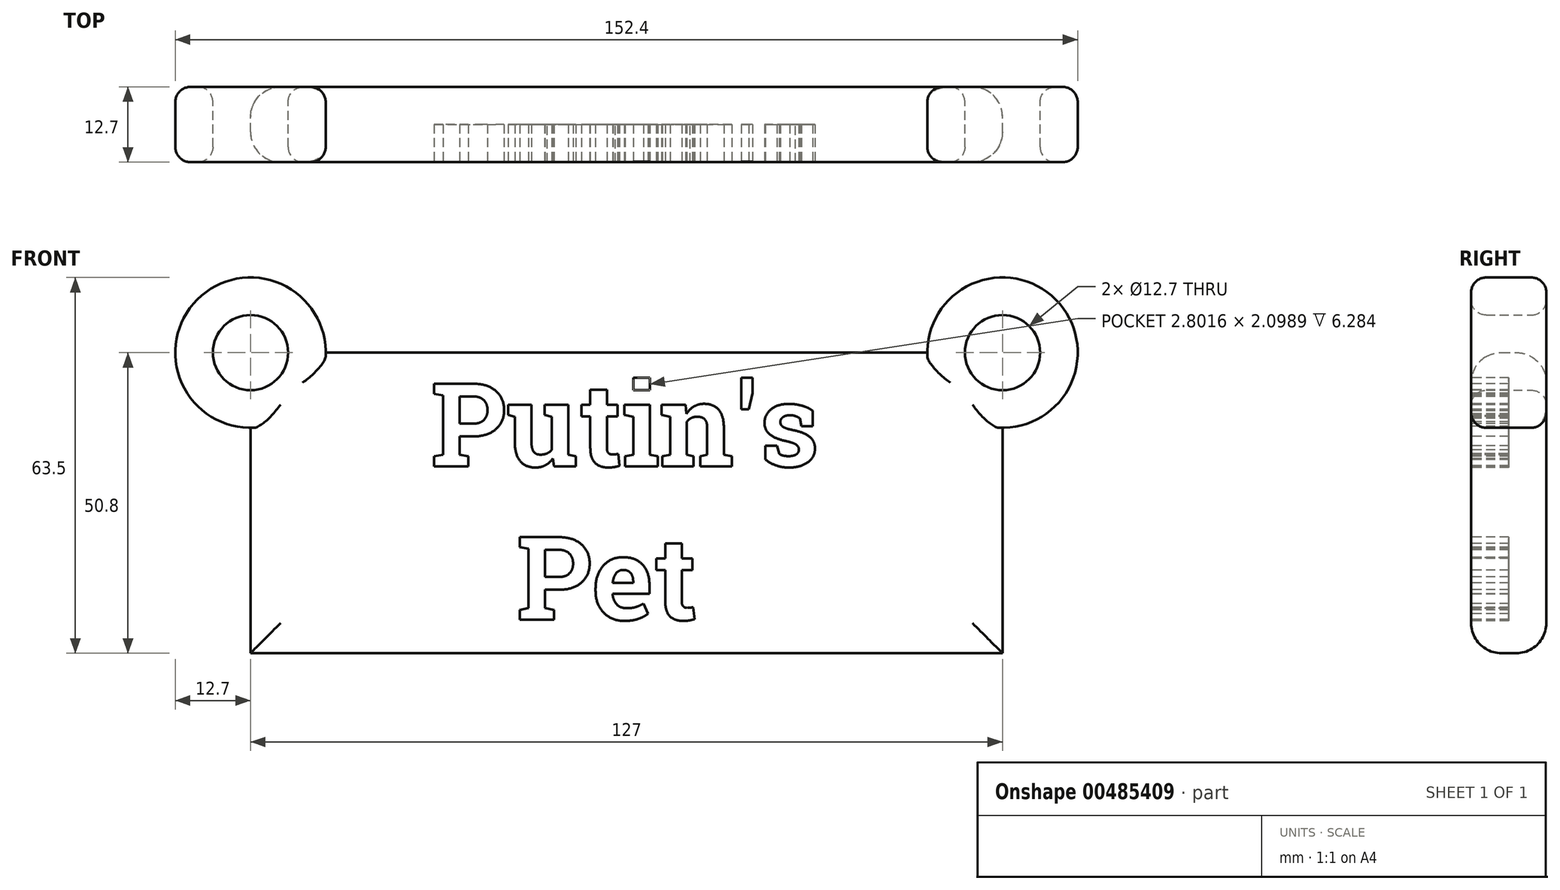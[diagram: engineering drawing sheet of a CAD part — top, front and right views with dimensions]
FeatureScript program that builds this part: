
annotation { "Feature Type Name" : "Feature", "Feature Type Description" : "" }
export const myFeature = defineFeature(function(context is Context, id is Id, definition is map)
    precondition{}
    {
        {
            var Q0;
            Q0=qCreatedBy(makeId("Front.planeOp"),FACE);
            var sketch = newSketch(context, id + "F0", { "sketchPlane" : qUnion([Q0])});
            skLineSegment(sketch, "E0.bottom", {"start": v(-127, 50.8) * mm, "end": v(0, 50.8) * mm});
            skLineSegment(sketch, "E0.top", {"start": v(-127, 0) * mm, "end": v(0, 0) * mm});
            skLineSegment(sketch, "E0.left", {"start": v(-127, 50.8) * mm, "end": v(-127, 0) * mm});
            skLineSegment(sketch, "E0.right", {"start": v(0, 50.8) * mm, "end": v(0, 0) * mm});
            skCircle(sketch, "E1", {"center": v(-127, 50.8) * mm, "radius": 6.35 * mm});
            skCircle(sketch, "E2", {"center": v(0, 50.8) * mm, "radius": 12.7 * mm});
            skCircle(sketch, "E3", {"center": v(0, 50.8) * mm, "radius": 6.35 * mm});
            skCircle(sketch, "E4", {"center": v(-127, 50.8) * mm, "radius": 12.7 * mm});
            skSolve(sketch);
        }
        {
            var Q0;
            Q0=qSketchRegion(id+"F0",true);
            extrude(context, id + "F1", {"entities" : qUnion([Q0]), "depth" : 12.7 * mm});
        }
        {
            var Q0;
            Q0=makeQuery(id+"F1.opExtrude","CAP_FACE",FACE,{"disambiguationData":[OSD([sQuery(id+"F0.wireOp",EDGE,"E0.bottom"),sQuery(id+"F0.wireOp",EDGE,"E0.top"),sQuery(id+"F0.wireOp",EDGE,"E0.left"),sQuery(id+"F0.wireOp",EDGE,"E0.right"),sQuery(id+"F0.wireOp",EDGE,"E1"),sQuery(id+"F0.wireOp",EDGE,"E2"),sQuery(id+"F0.wireOp",EDGE,"E3"),sQuery(id+"F0.wireOp",EDGE,"E4")])],"isStart":false});
            var sketch = newSketch(context, id + "F2", { "sketchPlane" : qUnion([Q0])});
            skText(sketch, "E5", { "text": "Putin\'s \n   Pet", "fontName": "RobotoSlab-Bold.ttf"});
            const initialGuessF2  = {"E5": [-0.09652, 0.03158, 1, 0, 0.01414]};
            skSetInitialGuess(sketch, initialGuessF2);
            skSolve(sketch);
        }
        {
            var Q0;
            Q0=qSketchRegion(id+"F2",true);
            extrude(context, id + "F3", {"entities" : qUnion([Q0]), "operationType" : NewBodyOperationType.REMOVE, "oppositeDirection" : true, "depth" : 6.35 * mm});
        }
        {
            var Q0;
            Q0=makeQuery(id+"F1.opExtrude","CAP_EDGE",EDGE,{"disambiguationData":[OSD([sQuery(id+"F0.wireOp",EDGE,"E1")])],"isStart":false});
            var Q1;
            Q1=makeQuery(id+"F1.opExtrude","CAP_EDGE",EDGE,{"disambiguationData":[OSD([sQuery(id+"F0.wireOp",EDGE,"E3")])],"isStart":false});
            var Q2;
            Q2=makeQuery(id+"F1.opExtrude","CAP_EDGE",EDGE,{"disambiguationData":[OSD([sQuery(id+"F0.wireOp",EDGE,"E1")])],"isStart":true});
            var Q3;
            Q3=makeQuery(id+"F1.opExtrude","CAP_EDGE",EDGE,{"disambiguationData":[OSD([sQuery(id+"F0.wireOp",EDGE,"E3")])],"isStart":true});
            var Q4;
            Q4=makeQuery(id+"F1.opExtrude","CAP_EDGE",EDGE,{"disambiguationData":[OSD([sQuery(id+"F0.wireOp",EDGE,"E4")])],"isStart":false});
            var Q5;
            Q5=makeQuery(id+"F1.opExtrude","CAP_EDGE",EDGE,{"disambiguationData":[OSD([sQuery(id+"F0.wireOp",EDGE,"E4")])],"isStart":true});
            var Q6;
            Q6=makeQuery(id+"F1.opExtrude","CAP_EDGE",EDGE,{"disambiguationData":[OSD([sQuery(id+"F0.wireOp",EDGE,"E2")])],"isStart":true});
            var Q7;
            Q7=makeQuery(id+"F1.opExtrude","CAP_EDGE",EDGE,{"disambiguationData":[OSD([sQuery(id+"F0.wireOp",EDGE,"E2")])],"isStart":false});
            fillet(context, id + "F4", {"entities" : qUnion([Q0, Q1, Q2, Q3, Q4, Q5, Q6, Q7]), "radius" : 2.54 * mm, "tangentPropagation" : true, "allowEdgeOverflow" : false});
        }
        {
            var Q0;
            Q0=makeQuery(id+"F1.opExtrude","CAP_EDGE",EDGE,{"disambiguationData":[OSD([sQuery(id+"F0.wireOp",EDGE,"E0.bottom")])],"isStart":false});
            var Q1;
            Q1=makeQuery(id+"F1.opExtrude","CAP_EDGE",EDGE,{"disambiguationData":[OSD([sQuery(id+"F0.wireOp",EDGE,"E0.bottom")])],"isStart":true});
            var Q2;
            Q2=makeQuery(id+"F1.opExtrude","CAP_EDGE",EDGE,{"disambiguationData":[OSD([sQuery(id+"F0.wireOp",EDGE,"E0.right")])],"isStart":false});
            var Q3;
            Q3=makeQuery(id+"F1.opExtrude","CAP_EDGE",EDGE,{"disambiguationData":[OSD([sQuery(id+"F0.wireOp",EDGE,"E0.right")])],"isStart":true});
            var Q4;
            Q4=makeQuery(id+"F1.opExtrude","CAP_EDGE",EDGE,{"disambiguationData":[OSD([sQuery(id+"F0.wireOp",EDGE,"E0.top")])],"isStart":false});
            var Q5;
            Q5=makeQuery(id+"F1.opExtrude","CAP_EDGE",EDGE,{"disambiguationData":[OSD([sQuery(id+"F0.wireOp",EDGE,"E0.left")])],"isStart":false});
            var Q6;
            Q6=makeQuery(id+"F1.opExtrude","CAP_EDGE",EDGE,{"disambiguationData":[OSD([sQuery(id+"F0.wireOp",EDGE,"E0.top")])],"isStart":true});
            var Q7;
            Q7=makeQuery(id+"F1.opExtrude","CAP_EDGE",EDGE,{"disambiguationData":[OSD([sQuery(id+"F0.wireOp",EDGE,"E0.left")])],"isStart":true});
            fillet(context, id + "F5", {"entities" : qUnion([Q0, Q1, Q2, Q3, Q4, Q5, Q6, Q7]), "radius" : 5.08 * mm, "tangentPropagation" : true, "allowEdgeOverflow" : false});
        }
    });
